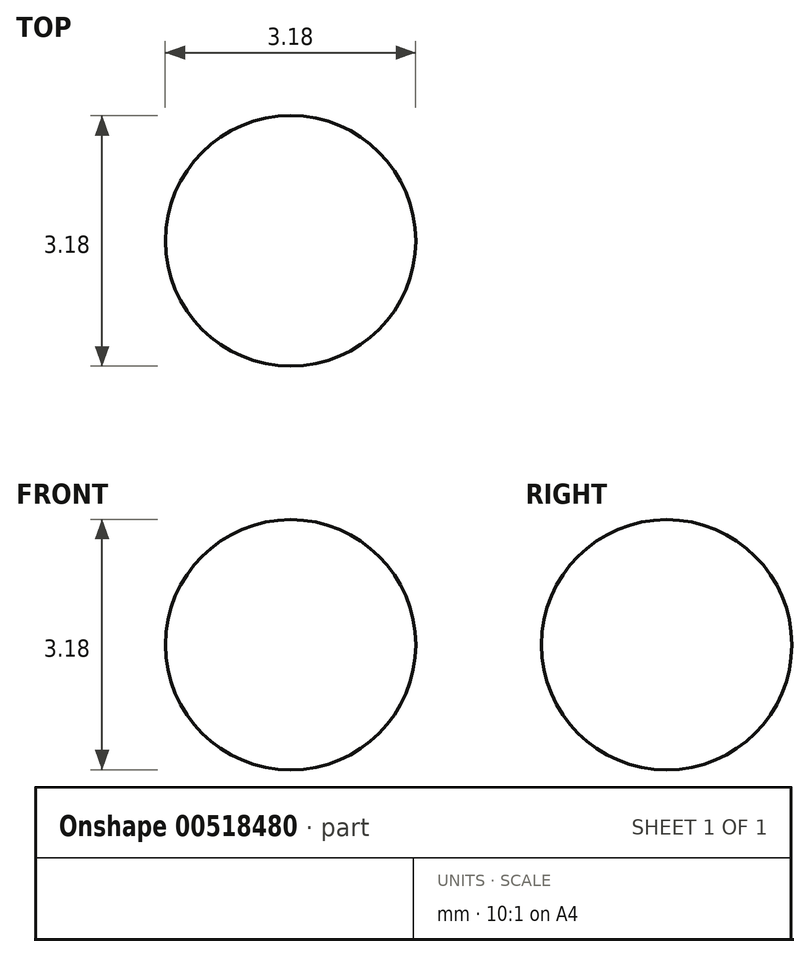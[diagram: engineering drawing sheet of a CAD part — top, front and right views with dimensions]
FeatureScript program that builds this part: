
annotation { "Feature Type Name" : "Feature", "Feature Type Description" : "" }
export const myFeature = defineFeature(function(context is Context, id is Id, definition is map)
    precondition{}
    {
        {
            var Q0;
            Q0=qCreatedBy(makeId("Front.planeOp"),FACE);
            var sketch = newSketch(context, id + "F0", { "sketchPlane" : qUnion([Q0])});
            skLineSegment(sketch, "E0", {"start": v(-6.16, -5.21) * mm, "end": v(-6.16, -8.4) * mm});
            skArc(sketch, "E1", {"start": v(-6.16, -8.4) * mm, "mid": v(-4.57, -6.8) * mm, "end": v(-6.16, -5.21) * mm});
            skLineSegment(sketch, "E2", {"start": v(-6.16, -5) * mm, "end": v(-6.16, -8.65) * mm, "construction": true});
            skSolve(sketch);
        }
        {
            var Q0;
            Q0=makeQuery(id+"F0.imprint","IMPRINT",FACE,{"disambiguationData":[TD([[makeQuery(id+"F0.imprint","IMPRINT",EDGE,{"derivedFrom":sQuery(id+"F0.wireOp",EDGE,"E0")}),1.0]])]});
            var Q1;
            Q1=sQuery(id+"F0.wireOp",EDGE,"E2");
            revolve(context, id + "F1", {"entities" : qUnion([Q0]), "axis" : qUnion([Q1]), "revolveType" : RevolveType.FULL});
        }
    });
